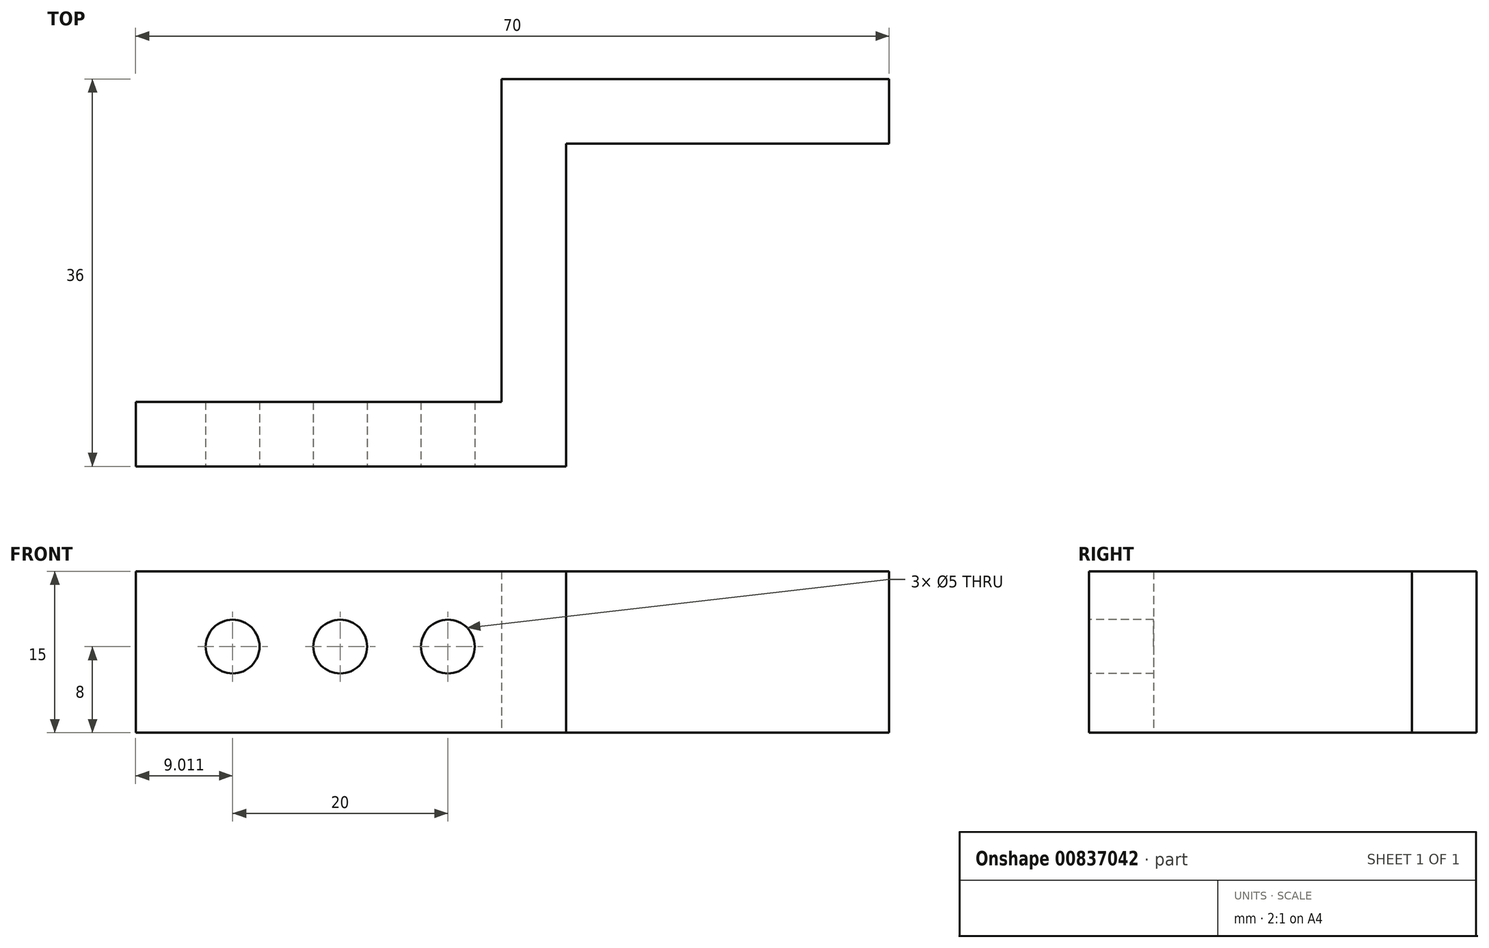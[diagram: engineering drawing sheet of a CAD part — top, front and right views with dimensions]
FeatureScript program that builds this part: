
annotation { "Feature Type Name" : "Feature", "Feature Type Description" : "" }
export const myFeature = defineFeature(function(context is Context, id is Id, definition is map)
    precondition{}
    {
        {
            var Q0;
            Q0=qCreatedBy(makeId("Top.planeOp"),FACE);
            var sketch = newSketch(context, id + "F0", { "sketchPlane" : qUnion([Q0])});
            skLineSegment(sketch, "E0", {"start": v(-19.79, -20.07) * mm, "end": v(14.21, -20.07) * mm});
            skLineSegment(sketch, "E1", {"start": v(14.21, -20.07) * mm, "end": v(14.21, 9.93) * mm});
            skLineSegment(sketch, "E2", {"start": v(14.21, 9.93) * mm, "end": v(50.21, 9.93) * mm});
            skLineSegment(sketch, "E3", {"start": v(50.21, 9.93) * mm, "end": v(50.21, 3.93) * mm});
            skLineSegment(sketch, "E4", {"start": v(50.21, 3.93) * mm, "end": v(20.21, 3.93) * mm});
            skLineSegment(sketch, "E5", {"start": v(20.21, 3.93) * mm, "end": v(20.21, -26.07) * mm});
            skLineSegment(sketch, "E6", {"start": v(20.21, -26.07) * mm, "end": v(-19.79, -26.07) * mm});
            skLineSegment(sketch, "E7", {"start": v(-19.79, -26.07) * mm, "end": v(-19.79, -20.07) * mm});
            skSolve(sketch);
        }
        {
            var Q0;
            Q0 = qSketchRegion(id + "F0", true);
            extrude(context, id + "F1", {"entities" : qUnion([Q0]), "depth" : 15 * mm, "offsetDistance" : 25 * mm});
        }
        {
            var Q0;
            Q0=makeQuery(id+"F1.opExtrude","SWEPT_FACE",FACE,{"disambiguationData":[OSD([sQuery(id+"F0.wireOp",EDGE,"E6")])]});
            var sketch = newSketch(context, id + "F2", { "sketchPlane" : qUnion([Q0])});
            skPoint(sketch, "E8", {"position": v(9.22, 8) * mm});
            skPoint(sketch, "E9", {"position": v(-0.78, 8) * mm});
            skPoint(sketch, "E10", {"position": v(-10.78, 8) * mm});
            skSolve(sketch);
        }
        {
            var Q0;
            Q0=sQuery(id+"F2.wireOp",VERTEX,"E8");
            var Q1;
            Q1=sQuery(id+"F2.wireOp",VERTEX,"E9");
            var Q2;
            Q2=sQuery(id+"F2.wireOp",VERTEX,"E10");
            var Q3;
            Q3=makeQuery(id+"F1.opExtrude","SWEPT_BODY",BODY,{"disambiguationData":[OSD([sQuery(id+"F0.wireOp",EDGE,"E0"),sQuery(id+"F0.wireOp",EDGE,"E1"),sQuery(id+"F0.wireOp",EDGE,"E2"),sQuery(id+"F0.wireOp",EDGE,"E3"),sQuery(id+"F0.wireOp",EDGE,"E4"),sQuery(id+"F0.wireOp",EDGE,"E5"),sQuery(id+"F0.wireOp",EDGE,"E6"),sQuery(id+"F0.wireOp",EDGE,"E7")])]});
            hole(context, id + "F3", {"style" : HoleStyle.SIMPLE, "endStyle" : HoleEndStyle.THROUGH, "holeDiameter" : 5 * mm, "majorDiameter" : 5 * mm, "isTappedThrough" : true, "tappedDepth" : 12 * mm, "tapClearance" : 3, "locations" : qUnion([Q0, Q1, Q2]), "scope" : qUnion([Q3])});
        }
    });
